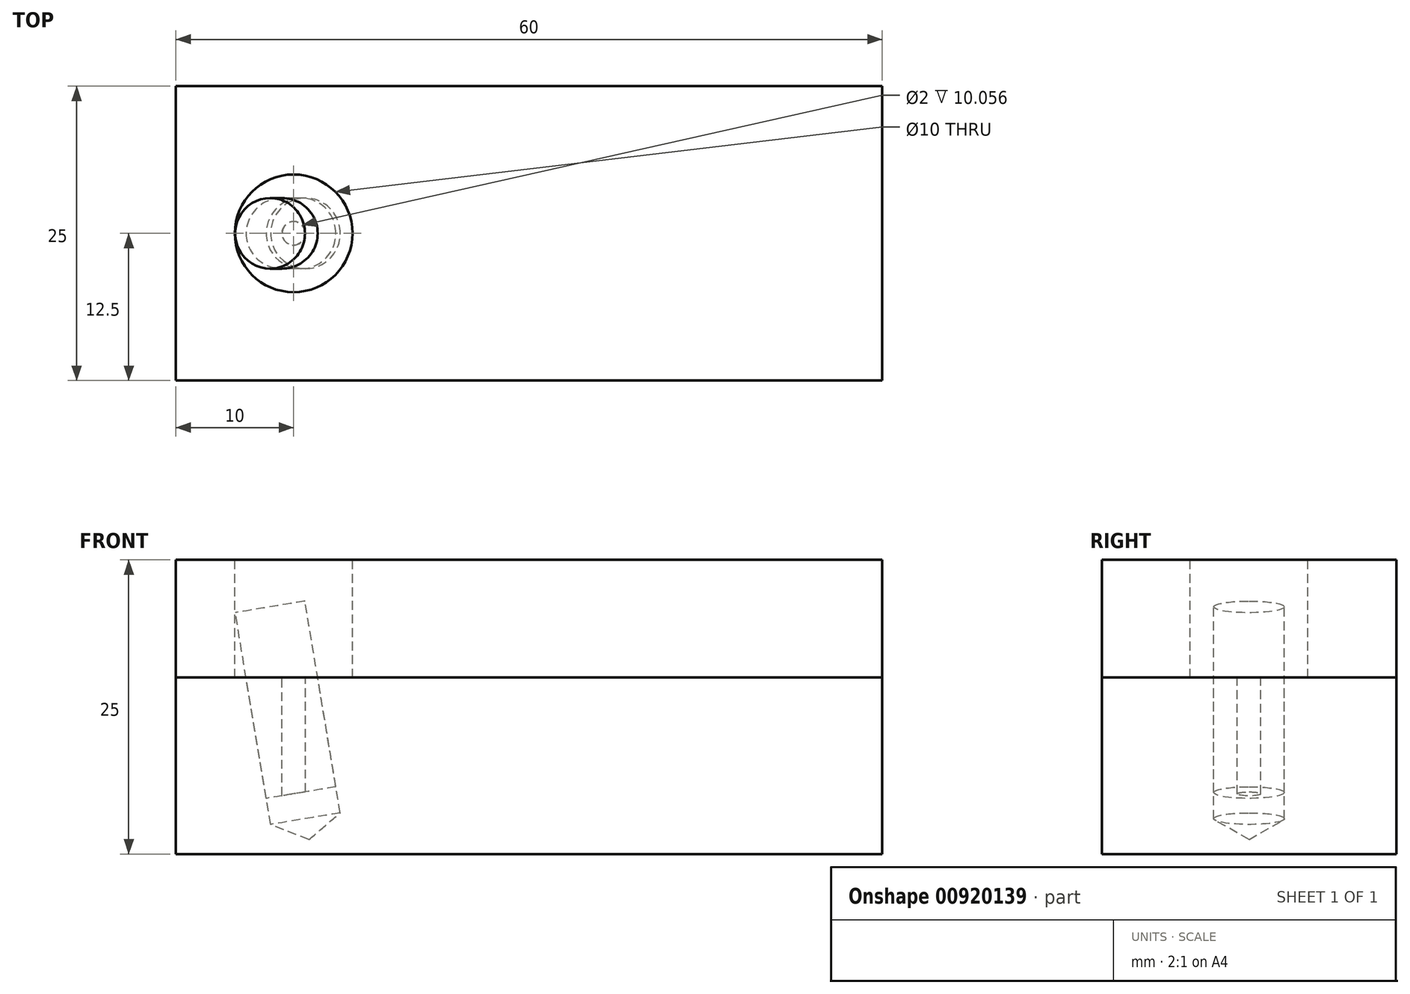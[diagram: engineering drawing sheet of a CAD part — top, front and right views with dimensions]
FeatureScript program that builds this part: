
annotation { "Feature Type Name" : "Feature", "Feature Type Description" : "" }
export const myFeature = defineFeature(function(context is Context, id is Id, definition is map)
    precondition{}
    {
        {
            var Q0;
            Q0=qCreatedBy(makeId("Front.planeOp"),FACE);
            var sketch = newSketch(context, id + "F0", { "sketchPlane" : qUnion([Q0])});
            skLineSegment(sketch, "E0.bottom", {"start": v(-30, 0) * mm, "end": v(30, 0) * mm});
            skLineSegment(sketch, "E0.top", {"start": v(-30, -15) * mm, "end": v(30, -15) * mm});
            skLineSegment(sketch, "E0.left", {"start": v(-30, 0) * mm, "end": v(-30, -15) * mm});
            skLineSegment(sketch, "E0.right", {"start": v(30, 0) * mm, "end": v(30, -15) * mm});
            skSolve(sketch);
        }
        {
            var Q0;
            Q0=qSketchRegion(id+"F0",true);
            extrude(context, id + "F1", {"entities" : qUnion([Q0]), "endBound" : BoundingType.SYMMETRIC, "depth" : 25 * mm, "offsetDistance" : 25 * mm});
        }
        {
            var Q0;
            Q0=qCreatedBy(makeId("Front.planeOp"),FACE);
            var sketch = newSketch(context, id + "F2", { "sketchPlane" : qUnion([Q0])});
            skLineSegment(sketch, "E1.bottom", {"start": v(-21, 0) * mm, "end": v(-19, 0) * mm, "construction": true});
            skLineSegment(sketch, "E1.top", {"start": v(-21, -12) * mm, "end": v(-19, -12) * mm, "construction": true});
            skLineSegment(sketch, "E1.left", {"start": v(-21, 0) * mm, "end": v(-21, -12) * mm, "construction": true});
            skLineSegment(sketch, "E1.right", {"start": v(-19, 0) * mm, "end": v(-19, -12) * mm, "construction": true});
            skLineSegment(sketch, "E2.bottom", {"start": v(-20, 0) * mm, "end": v(-20, 0) * mm});
            skLineSegment(sketch, "E2.top", {"start": v(-20, -12) * mm, "end": v(-20, -12) * mm});
            skLineSegment(sketch, "E2.left", {"start": v(-20, 0) * mm, "end": v(-20, -12) * mm, "construction": true});
            skLineSegment(sketch, "E2.right", {"start": v(-20, 0) * mm, "end": v(-20, -12) * mm, "construction": true});
            skLineSegment(sketch, "E3", {"start": v(-18.7, -13.78) * mm, "end": v(-22, 6) * mm});
            skLineSegment(sketch, "E4", {"start": v(-22, 6) * mm, "end": v(-24.96, 5.5) * mm});
            skLineSegment(sketch, "E5", {"start": v(-24.96, 5.5) * mm, "end": v(-21.96, -12.5) * mm});
            skLineSegment(sketch, "E6", {"start": v(-21.96, -12.5) * mm, "end": v(-18.7, -13.78) * mm});
            skLineSegment(sketch, "E7", {"start": v(-21.96, -12.5) * mm, "end": v(-19, -12) * mm, "construction": true});
            skSolve(sketch);
        }
        {
            var Q0;
            Q0=makeQuery(id+"F2.imprint","IMPRINT",FACE,{"disambiguationData":[TD([[makeQuery(id+"F2.imprint","IMPRINT",EDGE,{"derivedFrom":sQuery(id+"F2.wireOp",EDGE,"E3")}),1.0]])]});
            var Q1;
            Q1=sQuery(id+"F2.wireOp",EDGE,"E3");
            revolve(context, id + "F3", {"operationType" : NewBodyOperationType.REMOVE, "surfaceOperationType" : NewSurfaceOperationType.NEW, "entities" : qUnion([Q0]), "axis" : qUnion([Q1]), "revolveType" : RevolveType.FULL, "oppositeDirection" : true});
        }
        {
            var Q0;
            Q0=qCreatedBy(makeId("Front.planeOp"),FACE);
            var sketch = newSketch(context, id + "F4", { "sketchPlane" : qUnion([Q0])});
            skLineSegment(sketch, "E8.bottom", {"start": v(-21, 0) * mm, "end": v(-20, 0) * mm});
            skLineSegment(sketch, "E8.top", {"start": v(-21, -12) * mm, "end": v(-20, -12) * mm});
            skLineSegment(sketch, "E8.left", {"start": v(-21, 0) * mm, "end": v(-21, -12) * mm});
            skLineSegment(sketch, "E8.right", {"start": v(-20, 0) * mm, "end": v(-20, -12) * mm});
            skSolve(sketch);
        }
        {
            var Q0;
            Q0=qSketchRegion(id+"F4",true);
            var Q1;
            Q1=sQuery(id+"F4.wireOp",EDGE,"E8.right");
            revolve(context, id + "F5", {"surfaceOperationType" : NewSurfaceOperationType.NEW, "entities" : qUnion([Q0]), "axis" : qUnion([Q1]), "revolveType" : RevolveType.FULL});
        }
        {
            var Q0;
            Q0=qCreatedBy(makeId("Front.planeOp"),FACE);
            var sketch = newSketch(context, id + "F6", { "sketchPlane" : qUnion([Q0])});
            skLineSegment(sketch, "E9.bottom", {"start": v(-30, 0) * mm, "end": v(30, 0) * mm});
            skLineSegment(sketch, "E9.top", {"start": v(-30, 10) * mm, "end": v(30, 10) * mm});
            skLineSegment(sketch, "E9.left", {"start": v(-30, 0) * mm, "end": v(-30, 10) * mm});
            skLineSegment(sketch, "E9.right", {"start": v(30, 0) * mm, "end": v(30, 10) * mm});
            skSolve(sketch);
        }
        {
            var Q0;
            Q0=qSketchRegion(id+"F6",true);
            extrude(context, id + "F7", {"entities" : qUnion([Q0]), "endBound" : BoundingType.SYMMETRIC, "depth" : 25 * mm, "offsetDistance" : 25 * mm});
        }
        {
            var Q0;
            Q0=qCreatedBy(makeId("Front.planeOp"),FACE);
            var sketch = newSketch(context, id + "F8", { "sketchPlane" : qUnion([Q0])});
            skLineSegment(sketch, "E10.bottom", {"start": v(-20, 0) * mm, "end": v(-25, 0) * mm});
            skLineSegment(sketch, "E10.top", {"start": v(-20, 10) * mm, "end": v(-25, 10) * mm});
            skLineSegment(sketch, "E10.left", {"start": v(-20, 0) * mm, "end": v(-20, 10) * mm});
            skLineSegment(sketch, "E10.right", {"start": v(-25, 0) * mm, "end": v(-25, 10) * mm});
            skSolve(sketch);
        }
        {
            var Q0;
            Q0=qSketchRegion(id+"F8",true);
            var Q1;
            Q1=sQuery(id+"F8.wireOp",EDGE,"E10.left");
            revolve(context, id + "F9", {"operationType" : NewBodyOperationType.REMOVE, "surfaceOperationType" : NewSurfaceOperationType.NEW, "entities" : qUnion([Q0]), "axis" : qUnion([Q1]), "revolveType" : RevolveType.FULL, "oppositeDirection" : true});
        }
        {
            var Q0;
            Q0=qCreatedBy(makeId("Front.planeOp"),FACE);
            var sketch = newSketch(context, id + "F10", { "sketchPlane" : qUnion([Q0])});
            skLineSegment(sketch, "E11", {"start": v(-22.33, -10.28) * mm, "end": v(-24.96, 5.5) * mm});
            skLineSegment(sketch, "E12", {"start": v(-24.96, 5.5) * mm, "end": v(-22, 6) * mm});
            skLineSegment(sketch, "E13", {"start": v(-22, 6) * mm, "end": v(-19.37, -9.78) * mm});
            skLineSegment(sketch, "E14", {"start": v(-19.37, -9.78) * mm, "end": v(-22.33, -10.28) * mm});
            skSolve(sketch);
        }
        {
            var Q0;
            Q0=makeQuery(id+"F10.imprint","IMPRINT",FACE,{"disambiguationData":[TD([[makeQuery(id+"F10.imprint","IMPRINT",EDGE,{"derivedFrom":sQuery(id+"F10.wireOp",EDGE,"E11")}),-1.0]])]});
            var Q1;
            Q1=sQuery(id+"F10.wireOp",EDGE,"E13");
            revolve(context, id + "F11", {"surfaceOperationType" : NewSurfaceOperationType.NEW, "entities" : qUnion([Q0]), "axis" : qUnion([Q1]), "revolveType" : RevolveType.FULL});
        }
        {
            var Q0;
            Q0=qCreatedBy(makeId("Front.planeOp"),FACE);
            var sketch = newSketch(context, id + "F12", { "sketchPlane" : qUnion([Q0])});
            skLineSegment(sketch, "E15.bottom", {"start": v(-21, -12) * mm, "end": v(-20, -12) * mm});
            skLineSegment(sketch, "E15.top", {"start": v(-21, 0) * mm, "end": v(-20, 0) * mm});
            skLineSegment(sketch, "E15.left", {"start": v(-21, -12) * mm, "end": v(-21, 0) * mm});
            skLineSegment(sketch, "E16", {"start": v(-20, -12) * mm, "end": v(-20, 0) * mm});
            skPoint(sketch, "E17.orphan", {"position": v(-19, -12) * mm});
            skSolve(sketch);
        }
        {
            var Q0;
            Q0=qSketchRegion(id+"F12",true);
            var Q1;
            Q1=sQuery(id+"F12.wireOp",EDGE,"E16");
            revolve(context, id + "F13", {"operationType" : NewBodyOperationType.REMOVE, "surfaceOperationType" : NewSurfaceOperationType.NEW, "entities" : qUnion([Q0]), "axis" : qUnion([Q1]), "revolveType" : RevolveType.FULL, "oppositeDirection" : true});
        }
    });
